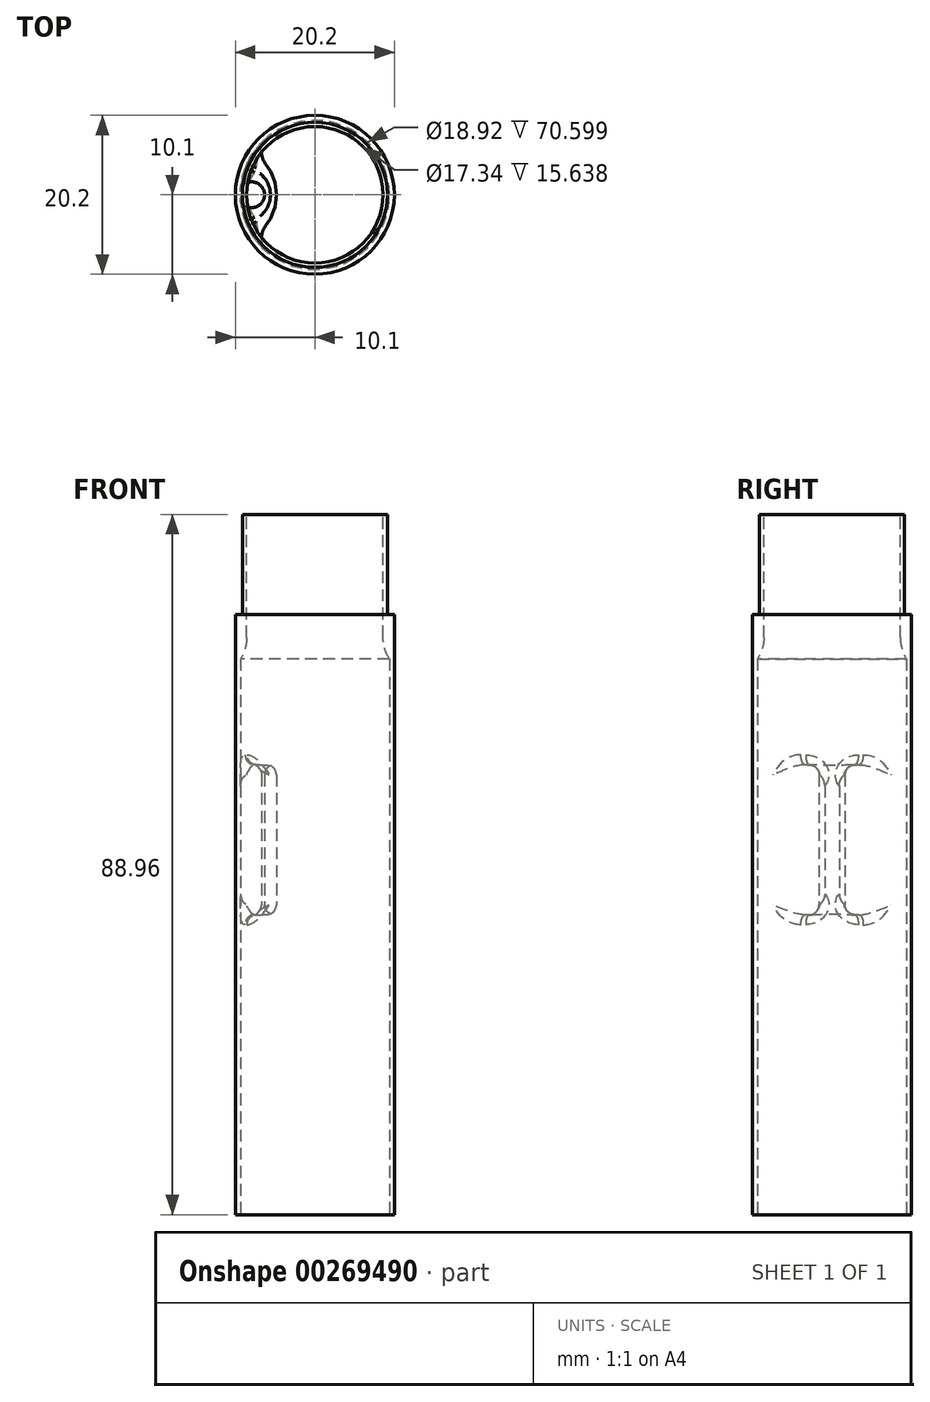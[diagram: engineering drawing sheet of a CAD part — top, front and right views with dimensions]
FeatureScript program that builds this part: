
annotation { "Feature Type Name" : "Feature", "Feature Type Description" : "" }
export const myFeature = defineFeature(function(context is Context, id is Id, definition is map)
    precondition{}
    {
        {
            var Q0;
            Q0=qCreatedBy(makeId("Top.planeOp"),FACE);
            var sketch = newSketch(context, id + "F0", { "sketchPlane" : qUnion([Q0])});
            skCircle(sketch, "E0", {"center": v(0, 0) * mm, "radius": 10.1 * mm});
            skCircle(sketch, "E1", {"center": v(0, 0) * mm, "radius": 9.46 * mm});
            skSolve(sketch);
        }
        {
            var Q0;
            Q0 = qSketchRegion(id + "F0", true);
            extrude(context, id + "F1", {"entities" : qUnion([Q0]), "depth" : 76.26 * mm});
        }
        {
            var Q0;
            Q0=makeQuery(id+"F1.opExtrude","CAP_FACE",FACE,{"disambiguationData":[OSD([sQuery(id+"F0.wireOp",EDGE,"E0"),sQuery(id+"F0.wireOp",EDGE,"E1")])],"isStart":false});
            var sketch = newSketch(context, id + "F2", { "sketchPlane" : qUnion([Q0])});
            skCircle(sketch, "E2", {"center": v(0, 0) * mm, "radius": 9.46 * mm});
            skCircle(sketch, "E3", {"center": v(0, 0) * mm, "radius": 8.67 * mm});
            skSolve(sketch);
        }
        {
            var Q0;
            Q0 = qSketchRegion(id + "F2", true);
            extrude(context, id + "F3", {"entities" : qUnion([Q0]), "operationType" : NewBodyOperationType.ADD, "oppositeDirection" : true, "depth" : 5.66 * mm});
        }
        {
            var Q0;
            Q0=qCreatedBy(makeId("Top.planeOp"),FACE);
            cPlane(context, id + "F4", {"entities" : qUnion([Q0]), "cplaneType" : CPlaneType.OFFSET, "offset" : 38.1 * mm, "width" : 152.4 * mm, "height" : 152.4 * mm});
        }
        {
            var Q0;
            Q0=qCreatedBy(id+"F4.planeOp",FACE);
            var sketch = newSketch(context, id + "F5", { "sketchPlane" : qUnion([Q0])});
            skArc(sketch, "E4", {"start": v(-8.36, -5.66) * mm, "mid": v(-4.88, 0) * mm, "end": v(-8.36, 5.66) * mm});
            skArc(sketch, "E5.0", {"start": v(-8.36, 5.66) * mm, "mid": v(-10.1, 0) * mm, "end": v(-8.36, -5.66) * mm});
            skCircle(sketch, "E6", {"center": v(-8.05, 0) * mm, "radius": 1.65 * mm});
            skSolve(sketch);
        }
        {
            var Q0;
            Q0 = qSketchRegion(id + "F5", true);
            extrude(context, id + "F6", {"entities" : qUnion([Q0]), "operationType" : NewBodyOperationType.ADD, "depth" : 19.05 * mm});
        }
        {
            var Q0;
            Q0=makeQuery(id+"F6.boolean.opBoolean","INTERSECT",EDGE,{"disambiguationData":[OD(0.0)],"derivedFrom":[makeQuery(id+"F1.opExtrude","SWEPT_FACE",FACE,{"disambiguationData":[OSD([sQuery(id+"F0.wireOp",EDGE,"E1")])]}),makeQuery(id+"F6.opExtrude","SWEPT_FACE",FACE,{"disambiguationData":[OSD([sQuery(id+"F5.wireOp",EDGE,"E4")])]})]});
            var Q1;
            Q1=makeQuery(id+"F6.boolean.opBoolean","INTERSECT",EDGE,{"disambiguationData":[OD(1.0)],"derivedFrom":[makeQuery(id+"F1.opExtrude","SWEPT_FACE",FACE,{"disambiguationData":[OSD([sQuery(id+"F0.wireOp",EDGE,"E1")])]}),makeQuery(id+"F6.opExtrude","SWEPT_FACE",FACE,{"disambiguationData":[OSD([sQuery(id+"F5.wireOp",EDGE,"E4")])]})]});
            fillet(context, id + "F7", {"entities" : qUnion([Q0, Q1]), "radius" : 2.54 * mm, "tangentPropagation" : true, "allowEdgeOverflow" : false});
        }
        {
            var Q0;
            Q0=makeQuery(id+"F3.boolean.opBoolean","MERGE",FACE,{"derivedFrom":[makeQuery(id+"F1.opExtrude","CAP_FACE",FACE,{"disambiguationData":[OSD([sQuery(id+"F0.wireOp",EDGE,"E0"),sQuery(id+"F0.wireOp",EDGE,"E1")])],"isStart":false}),makeQuery(id+"F3.opExtrude","CAP_FACE",FACE,{"disambiguationData":[OSD([sQuery(id+"F2.wireOp",EDGE,"E2"),sQuery(id+"F2.wireOp",EDGE,"E3")])],"isStart":true})]});
            var sketch = newSketch(context, id + "F8", { "sketchPlane" : qUnion([Q0])});
            skCircle(sketch, "E7.0", {"center": v(0, 0) * mm, "radius": 8.67 * mm});
            skCircle(sketch, "E8", {"center": v(0, 0) * mm, "radius": 9.2 * mm});
            skSolve(sketch);
        }
        {
            var Q0;
            Q0 = qSketchRegion(id + "F8", true);
            extrude(context, id + "F9", {"entities" : qUnion([Q0]), "operationType" : NewBodyOperationType.ADD, "depth" : 12.7 * mm});
        }
        {
            var Q0;
            Q0=makeQuery(id+"F3.opExtrude","CAP_EDGE",EDGE,{"disambiguationData":[OSD([sQuery(id+"F2.wireOp",EDGE,"E3")])],"isStart":false});
            fillet(context, id + "F10", {"entities" : qUnion([Q0]), "radius" : 5.08 * mm, "tangentPropagation" : true, "allowEdgeOverflow" : false});
        }
        {
            var Q0;
            Q0=makeQuery(id+"F6.opExtrude","CAP_FACE",FACE,{"disambiguationData":[OSD([sQuery(id+"F5.wireOp",EDGE,"E4"),sQuery(id+"F5.wireOp",EDGE,"E5.0"),sQuery(id+"F5.wireOp",EDGE,"E6")])],"isStart":true});
            var Q1;
            Q1=makeQuery(id+"F6.opExtrude","CAP_FACE",FACE,{"disambiguationData":[OSD([sQuery(id+"F5.wireOp",EDGE,"E4"),sQuery(id+"F5.wireOp",EDGE,"E5.0"),sQuery(id+"F5.wireOp",EDGE,"E6")])],"isStart":false});
            fillet(context, id + "F11", {"entities" : qUnion([Q0, Q1]), "radius" : 1.27 * mm, "tangentPropagation" : true, "allowEdgeOverflow" : false});
        }
    });
